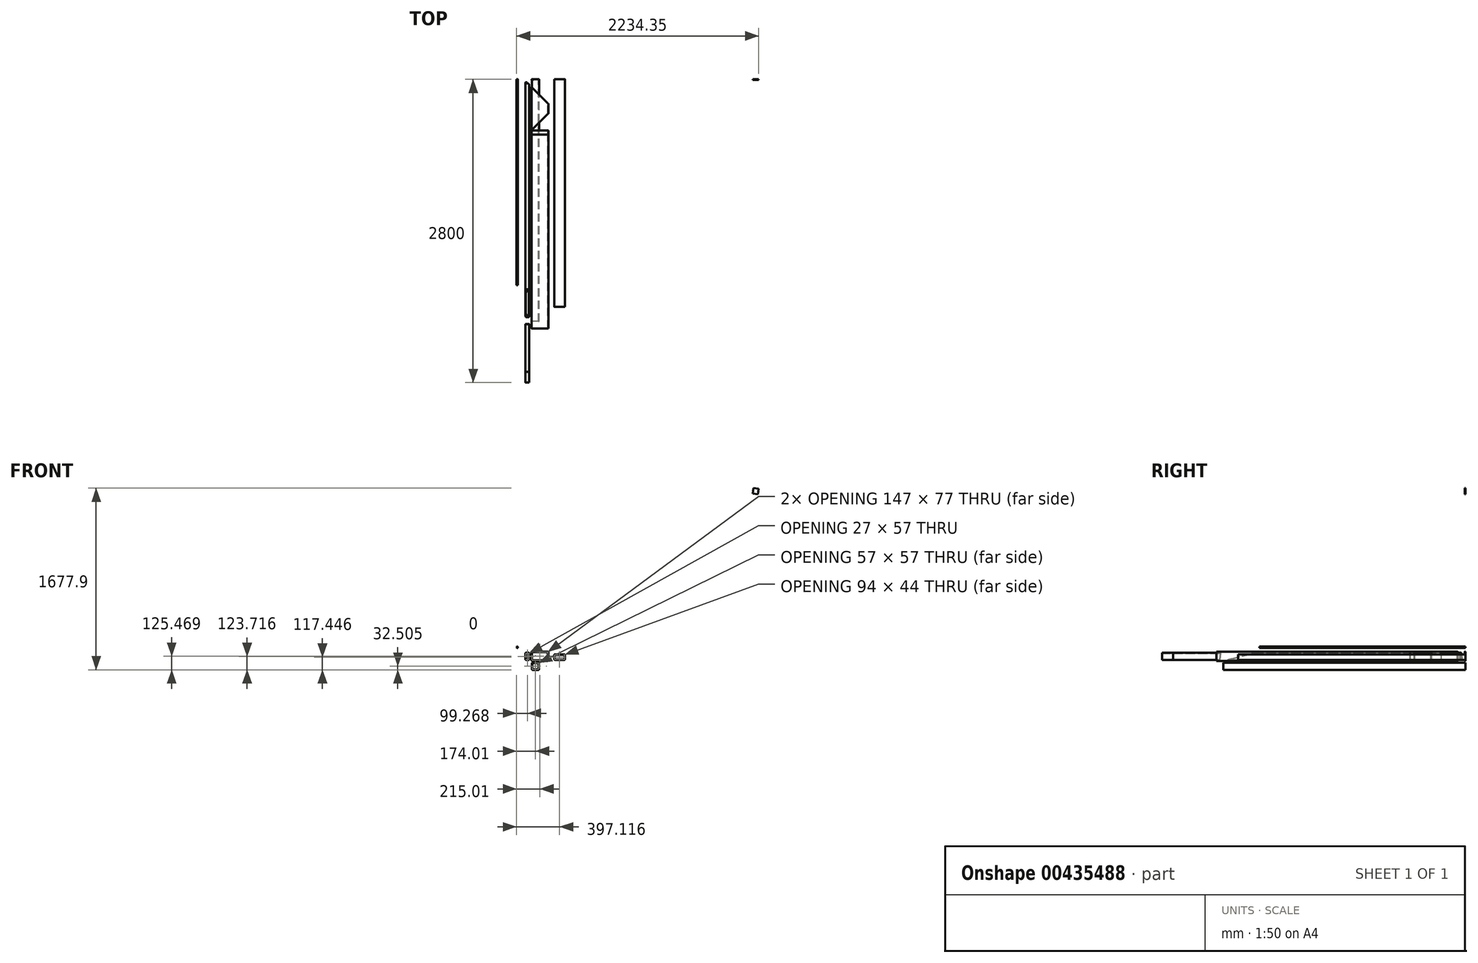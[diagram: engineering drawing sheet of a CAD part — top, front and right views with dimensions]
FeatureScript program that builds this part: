
annotation { "Feature Type Name" : "Feature", "Feature Type Description" : "" }
export const myFeature = defineFeature(function(context is Context, id is Id, definition is map)
    precondition{}
    {
        {
            var Q0;
            Q0=qCreatedBy(makeId("Front.planeOp"),FACE);
            var sketch = newSketch(context, id + "F0", { "sketchPlane" : qUnion([Q0])});
            skLineSegment(sketch, "E0.bottom", {"start": v(-54.74, 100.92) * mm, "end": v(-29.74, 100.92) * mm});
            skLineSegment(sketch, "E0.left", {"start": v(-59.74, 95.92) * mm, "end": v(-59.74, 40.92) * mm});
            skLineSegment(sketch, "E0.right", {"start": v(-24.74, 95.92) * mm, "end": v(-24.74, 40.92) * mm});
            skLineSegment(sketch, "E1.bottom", {"start": v(1, 27.67) * mm, "end": v(146, 27.67) * mm});
            skLineSegment(sketch, "E1.top", {"start": v(1, 112.67) * mm, "end": v(146, 112.67) * mm});
            skLineSegment(sketch, "E1.left", {"start": v(-4, 32.67) * mm, "end": v(-4, 107.67) * mm});
            skLineSegment(sketch, "E1.right", {"start": v(151, 32.67) * mm, "end": v(151, 107.67) * mm});
            skLineSegment(sketch, "E2.bottom", {"start": v(-50.74, 39.92) * mm, "end": v(-33.74, 39.92) * mm});
            skLineSegment(sketch, "E2.top", {"start": v(-50.74, 96.92) * mm, "end": v(-33.74, 96.92) * mm});
            skLineSegment(sketch, "E2.left", {"start": v(-55.74, 44.92) * mm, "end": v(-55.74, 91.92) * mm});
            skLineSegment(sketch, "E2.right", {"start": v(-28.74, 44.92) * mm, "end": v(-28.74, 91.92) * mm});
            skLineSegment(sketch, "E3", {"start": v(-54.74, 35.92) * mm, "end": v(-29.74, 35.92) * mm});
            skPoint(sketch, "E4.visualSharp", {"position": v(-59.74, 35.92) * mm});
            skArc(sketch, "E4.filletArc", {"start": v(-59.74, 40.92) * mm, "mid": v(-58.28, 37.38) * mm, "end": v(-54.74, 35.92) * mm});
            skPoint(sketch, "E5.visualSharp", {"position": v(-24.74, 35.92) * mm});
            skArc(sketch, "E5.filletArc", {"start": v(-29.74, 35.92) * mm, "mid": v(-26.2, 37.38) * mm, "end": v(-24.74, 40.92) * mm});
            skPoint(sketch, "E6.visualSharp", {"position": v(-28.74, 39.92) * mm});
            skArc(sketch, "E6.filletArc", {"start": v(-33.74, 39.92) * mm, "mid": v(-30.2, 41.38) * mm, "end": v(-28.74, 44.92) * mm});
            skPoint(sketch, "E7.visualSharp", {"position": v(-55.74, 39.92) * mm});
            skArc(sketch, "E7.filletArc", {"start": v(-55.74, 44.92) * mm, "mid": v(-54.28, 41.38) * mm, "end": v(-50.74, 39.92) * mm});
            skPoint(sketch, "E8.visualSharp", {"position": v(-55.74, 96.92) * mm});
            skArc(sketch, "E8.filletArc", {"start": v(-50.74, 96.92) * mm, "mid": v(-54.28, 95.45) * mm, "end": v(-55.74, 91.92) * mm});
            skPoint(sketch, "E9.visualSharp", {"position": v(-59.74, 100.92) * mm});
            skArc(sketch, "E9.filletArc", {"start": v(-54.74, 100.92) * mm, "mid": v(-58.28, 99.45) * mm, "end": v(-59.74, 95.92) * mm});
            skPoint(sketch, "E10.visualSharp", {"position": v(-28.74, 96.92) * mm});
            skArc(sketch, "E10.filletArc", {"start": v(-28.74, 91.92) * mm, "mid": v(-30.2, 95.45) * mm, "end": v(-33.74, 96.92) * mm});
            skPoint(sketch, "E11.visualSharp", {"position": v(-24.74, 100.92) * mm});
            skArc(sketch, "E11.filletArc", {"start": v(-24.74, 95.92) * mm, "mid": v(-26.2, 99.45) * mm, "end": v(-29.74, 100.92) * mm});
            skLineSegment(sketch, "E12.bottom", {"start": v(142, 108.67) * mm, "end": v(5, 108.67) * mm});
            skLineSegment(sketch, "E12.top", {"start": v(142, 31.67) * mm, "end": v(5, 31.67) * mm});
            skLineSegment(sketch, "E12.left", {"start": v(147, 103.67) * mm, "end": v(147, 36.67) * mm});
            skLineSegment(sketch, "E12.right", {"start": v(0, 103.67) * mm, "end": v(0, 36.67) * mm});
            skPoint(sketch, "E13.visualSharp", {"position": v(147, 108.67) * mm});
            skArc(sketch, "E13.filletArc", {"start": v(147, 103.67) * mm, "mid": v(145.54, 107.2) * mm, "end": v(142, 108.67) * mm});
            skPoint(sketch, "E14.visualSharp", {"position": v(151, 112.67) * mm});
            skArc(sketch, "E14.filletArc", {"start": v(151, 107.67) * mm, "mid": v(149.54, 111.2) * mm, "end": v(146, 112.67) * mm});
            skPoint(sketch, "E15.visualSharp", {"position": v(147, 31.67) * mm});
            skArc(sketch, "E15.filletArc", {"start": v(142, 31.67) * mm, "mid": v(145.54, 33.13) * mm, "end": v(147, 36.67) * mm});
            skPoint(sketch, "E16.visualSharp", {"position": v(151, 27.67) * mm});
            skArc(sketch, "E16.filletArc", {"start": v(146, 27.67) * mm, "mid": v(149.54, 29.13) * mm, "end": v(151, 32.67) * mm});
            skPoint(sketch, "E17.visualSharp", {"position": v(0, 31.67) * mm});
            skArc(sketch, "E17.filletArc", {"start": v(0, 36.67) * mm, "mid": v(1.46, 33.13) * mm, "end": v(5, 31.67) * mm});
            skPoint(sketch, "E18.visualSharp", {"position": v(-4, 27.67) * mm});
            skArc(sketch, "E18.filletArc", {"start": v(-4, 32.67) * mm, "mid": v(-2.54, 29.13) * mm, "end": v(1, 27.67) * mm});
            skPoint(sketch, "E19.visualSharp", {"position": v(0, 108.67) * mm});
            skArc(sketch, "E19.filletArc", {"start": v(5, 108.67) * mm, "mid": v(1.46, 107.2) * mm, "end": v(0, 103.67) * mm});
            skPoint(sketch, "E20.visualSharp", {"position": v(-4, 112.67) * mm});
            skArc(sketch, "E20.filletArc", {"start": v(1, 112.67) * mm, "mid": v(-2.54, 111.2) * mm, "end": v(-4, 107.67) * mm});
            skLineSegment(sketch, "E21.bottom", {"start": v(-105.6, 102.74) * mm, "end": v(-100.6, 102.74) * mm});
            skLineSegment(sketch, "E21.top", {"start": v(-105.6, 52.74) * mm, "end": v(-100.6, 52.74) * mm});
            skLineSegment(sketch, "E21.left", {"start": v(-105.6, 102.74) * mm, "end": v(-105.6, 52.74) * mm});
            skLineSegment(sketch, "E21.right", {"start": v(-100.6, 102.74) * mm, "end": v(-100.6, 52.74) * mm});
            skCircle(sketch, "E22", {"center": v(-135.5, 152.96) * mm, "radius": 6 * mm});
            skLineSegment(sketch, "E23", {"start": v(442.6, -372.53) * mm, "end": v(508.1, -372.53) * mm});
            skLineSegment(sketch, "E24", {"start": v(742.6, 1777.47) * mm, "end": v(710.1, 1777.47) * mm});
            skLineSegment(sketch, "E25", {"start": v(710.1, 1777.47) * mm, "end": v(775.1, 1777.47) * mm});
            skLineSegment(sketch, "E26", {"start": v(742.6, 1777.47) * mm, "end": v(775.1, 1777.47) * mm});
            skLineSegment(sketch, "E27", {"start": v(775.1, 1777.47) * mm, "end": v(710.1, 1777.47) * mm});
            skPoint(sketch, "E28.start.orphan", {"position": v(977.6, -372.53) * mm});
            skPoint(sketch, "E29.end.orphan", {"position": v(1042.6, -372.53) * mm});
            skLineSegment(sketch, "E30", {"start": v(742.6, 1777.47) * mm, "end": v(742.6, 1919.14) * mm});
            skLineSegment(sketch, "E31", {"start": v(742.6, 1919.14) * mm, "end": v(741.04, 1777.47) * mm});
            skPoint(sketch, "E32.end.orphan", {"position": v(508.1, -372.53) * mm});
            skPoint(sketch, "E33.trimOffspring.end.orphan", {"position": v(710.1, -1044.25) * mm});
            skLineSegment(sketch, "E34", {"start": v(1952.78, 1421.83) * mm, "end": v(2252.78, 1421.83) * mm});
            skLineSegment(sketch, "E35", {"start": v(2252.78, 1421.83) * mm, "end": v(2552.78, 1421.83) * mm});
            skLineSegment(sketch, "E36", {"start": v(2252.78, 3572.34) * mm, "end": v(2285.53, 3572.34) * mm});
            skLineSegment(sketch, "E37", {"start": v(2252.78, 3572.34) * mm, "end": v(2220.03, 3572.34) * mm});
            skLineSegment(sketch, "E38", {"start": v(2220.03, 3572.34) * mm, "end": v(1952.78, 1421.83) * mm});
            skLineSegment(sketch, "E39", {"start": v(2018.28, 1421.83) * mm, "end": v(2285.53, 3572.34) * mm});
            skLineSegment(sketch, "E40", {"start": v(2285.53, 3572.34) * mm, "end": v(2552.78, 1421.83) * mm});
            skLineSegment(sketch, "E41", {"start": v(2738.77, 1353.7) * mm, "end": v(2738.77, 1582.44) * mm});
            skLineSegment(sketch, "E42", {"start": v(2487.28, 1421.83) * mm, "end": v(2252.78, 3308.8) * mm});
            skLineSegment(sketch, "E43", {"start": v(2037.06, 1572.98) * mm, "end": v(2086.68, 1566.81) * mm});
            skLineSegment(sketch, "E44", {"start": v(2086.68, 1566.81) * mm, "end": v(2092.84, 1616.43) * mm});
            skLineSegment(sketch, "E45", {"start": v(2092.84, 1616.43) * mm, "end": v(2043.23, 1622.6) * mm});
            skLineSegment(sketch, "E46", {"start": v(2086.68, 1566.81) * mm, "end": v(2068.66, 1421.83) * mm});
            skLineSegment(sketch, "E47", {"start": v(2068.66, 1421.83) * mm, "end": v(2275.59, 3086.93) * mm});
            skLineSegment(sketch, "E48", {"start": v(2421.77, 1948.91) * mm, "end": v(2372.16, 1942.74) * mm});
            skLineSegment(sketch, "E49", {"start": v(2372.16, 1942.74) * mm, "end": v(2366, 1992.36) * mm});
            skLineSegment(sketch, "E50", {"start": v(2366, 1992.36) * mm, "end": v(2415.6, 1998.53) * mm});
            skLineSegment(sketch, "E51", {"start": v(2366, 1992.36) * mm, "end": v(2436.9, 1421.83) * mm});
            skLineSegment(sketch, "E52", {"start": v(2436.9, 1421.83) * mm, "end": v(2252.78, 2903.37) * mm});
            skSolve(sketch);
        }
        {
            var Q0;
            Q0=makeQuery(id+"F0.imprint","IMPRINT",FACE,{"disambiguationData":[TD([[makeQuery(id+"F0.imprint","IMPRINT",EDGE,{"derivedFrom":sQuery(id+"F0.wireOp",EDGE,"E1.bottom")}),1.0]])]});
            extrude(context, id + "F1", {"entities" : qUnion([Q0]), "depth" : 2300 * mm, "offsetDistance" : 25 * mm});
        }
        {
            var Q0;
            Q0=makeQuery(id+"F0.imprint","IMPRINT",FACE,{"disambiguationData":[TD([[makeQuery(id+"F0.imprint","IMPRINT",EDGE,{"derivedFrom":sQuery(id+"F0.wireOp",EDGE,"E0.bottom")}),-1.0]])]});
            extrude(context, id + "F2", {"entities" : qUnion([Q0]), "depth" : 2800 * mm});
        }
        {
            var Q0;
            Q0=makeQuery(id+"F0.imprint","IMPRINT",FACE,{"disambiguationData":[TD([[makeQuery(id+"F0.imprint","IMPRINT",EDGE,{"derivedFrom":sQuery(id+"F0.wireOp",EDGE,"E0.bottom")}),-1.0]])]});
            extrude(context, id + "F3", {"entities" : qUnion([Q0]), "depth" : 2700 * mm});
        }
        {
            var Q0;
            Q0=makeQuery(id+"F0.imprint","IMPRINT",FACE,{"disambiguationData":[TD([[makeQuery(id+"F0.imprint","IMPRINT",EDGE,{"derivedFrom":sQuery(id+"F0.wireOp",EDGE,"E0.bottom")}),-1.0]])]});
            extrude(context, id + "F4", {"entities" : qUnion([Q0]), "depth" : 2230 * mm});
        }
        {
            var Q0;
            Q0=makeQuery(id+"F0.imprint","IMPRINT",FACE,{"disambiguationData":[TD([[makeQuery(id+"F0.imprint","IMPRINT",EDGE,{"derivedFrom":sQuery(id+"F0.wireOp",EDGE,"E0.bottom")}),-1.0]])]});
            extrude(context, id + "F5", {"entities" : qUnion([Q0]), "depth" : 2200 * mm});
        }
        {
            var Q0;
            Q0=makeQuery(id+"F5.opExtrude","SWEPT_FACE",FACE,{"disambiguationData":[OSD([sQuery(id+"F0.wireOp",EDGE,"E0.right")])]});
            var sketch = newSketch(context, id + "F6", { "sketchPlane" : qUnion([Q0])});
            skLineSegment(sketch, "E53", {"start": v(-2188.64, 40.92) * mm, "end": v(-2149, 50.93) * mm});
            skLineSegment(sketch, "E54", {"start": v(-2149, 50.93) * mm, "end": v(-2188.64, 40.92) * mm});
            skLineSegment(sketch, "E55", {"start": v(-2239.78, 24.91) * mm, "end": v(-1867.66, 118.85) * mm});
            skLineSegment(sketch, "E56.top", {"start": v(-2239.78, 123.37) * mm, "end": v(-1867.66, 123.37) * mm});
            skLineSegment(sketch, "E56.left", {"start": v(-2239.78, 24.91) * mm, "end": v(-2239.78, 123.37) * mm});
            skLineSegment(sketch, "E56.right", {"start": v(-1867.66, 118.85) * mm, "end": v(-1867.66, 123.37) * mm});
            skLineSegment(sketch, "E57", {"start": v(-65.35, 40.92) * mm, "end": v(-65.35, 95.92) * mm});
            skLineSegment(sketch, "E58", {"start": v(-65.35, 95.92) * mm, "end": v(-59.5, 48.5) * mm});
            skSolve(sketch);
        }
        {
            var Q0;
            Q0 = qSketchRegion(id + "F6", true);
            extrude(context, id + "F7", {"entities" : qUnion([Q0]), "operationType" : NewBodyOperationType.REMOVE, "oppositeDirection" : true, "depth" : 65 * mm});
        }
        {
            var Q0;
            Q0=makeQuery(id+"F5.opExtrude","SWEPT_FACE",FACE,{"disambiguationData":[OSD([sQuery(id+"F0.wireOp",EDGE,"E3")])]});
            var sketch = newSketch(context, id + "F8", { "sketchPlane" : qUnion([Q0])});
            skLineSegment(sketch, "E59", {"start": v(-42.24, 2196.2) * mm, "end": v(-42.24, 29.2) * mm});
            skLineSegment(sketch, "E60", {"start": v(-42.24, 29.2) * mm, "end": v(-67.64, 29.2) * mm});
            skLineSegment(sketch, "E61.bottom", {"start": v(-67.64, 29.2) * mm, "end": v(-16.84, 29.2) * mm});
            skLineSegment(sketch, "E61.top", {"start": v(-67.64, -7.9) * mm, "end": v(-16.84, -7.9) * mm});
            skLineSegment(sketch, "E61.left", {"start": v(-67.64, 29.2) * mm, "end": v(-67.64, -7.9) * mm});
            skLineSegment(sketch, "E61.right", {"start": v(-16.84, 29.2) * mm, "end": v(-16.84, -7.9) * mm});
            skSolve(sketch);
        }
        {
            var Q0;
            Q0 = qSketchRegion(id + "F8", true);
            extrude(context, id + "F9", {"entities" : qUnion([Q0]), "operationType" : NewBodyOperationType.REMOVE, "oppositeDirection" : true, "depth" : 218 * mm});
        }
        {
            var Q0;
            Q0=makeQuery(id+"F5.opExtrude","SWEPT_FACE",FACE,{"disambiguationData":[OSD([sQuery(id+"F0.wireOp",EDGE,"E0.right")])]});
            var sketch = newSketch(context, id + "F10", { "sketchPlane" : qUnion([Q0])});
            skLineSegment(sketch, "E62", {"start": v(-29.2, 40.92) * mm, "end": v(-29.2, 35.92) * mm});
            skLineSegment(sketch, "E63", {"start": v(-29.2, 35.92) * mm, "end": v(-31.78, 56.74) * mm});
            skLineSegment(sketch, "E64", {"start": v(-29.2, 35.92) * mm, "end": v(-37.8, 105.2) * mm});
            skLineSegment(sketch, "E65", {"start": v(-37.8, 105.2) * mm, "end": v(-13.27, 108.25) * mm});
            skLineSegment(sketch, "E66", {"start": v(-13.27, 108.25) * mm, "end": v(-29.2, 35.92) * mm});
            skLineSegment(sketch, "E67", {"start": v(-2210.13, 148.78) * mm, "end": v(-2253.16, 154.06) * mm});
            skLineSegment(sketch, "E68", {"start": v(-2253.16, 154.06) * mm, "end": v(-2270.71, 11.1) * mm});
            skLineSegment(sketch, "E69", {"start": v(-2270.71, 11.1) * mm, "end": v(-2203.3, 2.83) * mm});
            skLineSegment(sketch, "E70", {"start": v(-2203.3, 2.83) * mm, "end": v(-2196.2, 35.92) * mm});
            skLineSegment(sketch, "E71", {"start": v(-2196.2, 35.92) * mm, "end": v(-2217.53, 208.7) * mm});
            skSolve(sketch);
        }
        {
            var Q0;
            Q0 = qSketchRegion(id + "F10", true);
            extrude(context, id + "F11", {"entities" : qUnion([Q0]), "operationType" : NewBodyOperationType.REMOVE, "oppositeDirection" : true, "depth" : 47.9 * mm});
        }
        {
            var Q0;
            Q0=makeQuery(id+"F0.imprint","IMPRINT",FACE,{"disambiguationData":[TD([[makeQuery(id+"F0.imprint","IMPRINT",EDGE,{"derivedFrom":sQuery(id+"F0.wireOp",EDGE,"E0.bottom")}),-1.0]])]});
            extrude(context, id + "F12", {"entities" : qUnion([Q0]), "depth" : 3000 * mm});
        }
        {
            var Q0;
            Q0 = qSketchRegion(id + "F10", true);
            extrude(context, id + "F13", {"entities" : qUnion([Q0]), "operationType" : NewBodyOperationType.REMOVE, "oppositeDirection" : true, "depth" : 73 * mm});
        }
        {
            var Q0;
            Q0=makeQuery(id+"F13.boolean.opBoolean","SPLIT",BODY,{"disambiguationData":[OD(0.0)],"derivedFrom":makeQuery(id+"F12.opExtrude","SWEPT_BODY",BODY,{"disambiguationData":[OSD([sQuery(id+"F0.wireOp",EDGE,"E0.bottom"),sQuery(id+"F0.wireOp",EDGE,"E0.left"),sQuery(id+"F0.wireOp",EDGE,"E0.right"),sQuery(id+"F0.wireOp",EDGE,"E2.bottom"),sQuery(id+"F0.wireOp",EDGE,"E2.top"),sQuery(id+"F0.wireOp",EDGE,"E2.left"),sQuery(id+"F0.wireOp",EDGE,"E2.right"),sQuery(id+"F0.wireOp",EDGE,"E3"),sQuery(id+"F0.wireOp",EDGE,"E4.filletArc"),sQuery(id+"F0.wireOp",EDGE,"E5.filletArc"),sQuery(id+"F0.wireOp",EDGE,"E6.filletArc"),sQuery(id+"F0.wireOp",EDGE,"E7.filletArc"),sQuery(id+"F0.wireOp",EDGE,"E8.filletArc"),sQuery(id+"F0.wireOp",EDGE,"E9.filletArc"),sQuery(id+"F0.wireOp",EDGE,"E10.filletArc"),sQuery(id+"F0.wireOp",EDGE,"E11.filletArc")])]})});
            deleteBodies(context, id + "F14", {"entities" : qUnion([Q0])});
        }
        {
            var Q0;
            Q0=makeQuery(id+"F0.imprint","IMPRINT",FACE,{"disambiguationData":[TD([[makeQuery(id+"F0.imprint","IMPRINT",EDGE,{"derivedFrom":sQuery(id+"F0.wireOp",EDGE,"E22")}),1.0]])]});
            extrude(context, id + "F15", {"entities" : qUnion([Q0]), "depth" : 1900.9 * mm});
        }
        {
            var Q0;
            {var subQ0=sQuery(id+"F0.wireOp",EDGE,"E43");Q0=makeQuery(id+"F0.imprint","IMPRINT",FACE,{"disambiguationData":[TD([[makeQuery(id+"F0.imprint","IMPRINT",EDGE,{"derivedFrom":subQ0}),1.0]])]});}
            extrude(context, id + "F16", {"entities" : qUnion([Q0]), "depth" : 5 * mm});
        }
        {
            var Q0;
            Q0=makeQuery(id+"F0.imprint","IMPRINT",FACE,{"disambiguationData":[TD([[makeQuery(id+"F0.imprint","IMPRINT",EDGE,{"derivedFrom":sQuery(id+"F0.wireOp",EDGE,"E1.bottom")}),1.0]])]});
            extrude(context, id + "F17", {"entities" : qUnion([Q0]), "depth" : 510 * mm});
        }
        {
            var Q0;
            Q0=makeQuery(id+"F17.opExtrude","SWEPT_FACE",FACE,{"disambiguationData":[OSD([sQuery(id+"F0.wireOp",EDGE,"E1.top")])]});
            var sketch = newSketch(context, id + "F18", { "sketchPlane" : qUnion([Q0])});
            skLineSegment(sketch, "E72", {"start": v(146, -220.74) * mm, "end": v(-59.9, -14.83) * mm});
            skLineSegment(sketch, "E73", {"start": v(146, -320.74) * mm, "end": v(-7.13, -473.86) * mm});
            skLineSegment(sketch, "E74", {"start": v(-7.13, -473.86) * mm, "end": v(185.32, -473.86) * mm});
            skLineSegment(sketch, "E75", {"start": v(185.32, -473.86) * mm, "end": v(185.32, 27.31) * mm});
            skLineSegment(sketch, "E76", {"start": v(185.32, 27.31) * mm, "end": v(-59.9, -14.83) * mm});
            skLineSegment(sketch, "E77", {"start": v(146, -220.74) * mm, "end": v(162.83, -237.57) * mm});
            skLineSegment(sketch, "E78", {"start": v(146, -320.74) * mm, "end": v(165.64, -301.1) * mm});
            skLineSegment(sketch, "E79", {"start": v(165.64, -301.1) * mm, "end": v(162.83, -237.57) * mm});
            skSolve(sketch);
        }
        {
            var Q0;
            Q0 = qSketchRegion(id + "F18", true);
            extrude(context, id + "F19", {"entities" : qUnion([Q0]), "operationType" : NewBodyOperationType.REMOVE, "oppositeDirection" : true, "depth" : 125 * mm});
        }
        {
            var Q0;
            Q0=qCreatedBy(makeId("Front.planeOp"),FACE);
            var sketch = newSketch(context, id + "F20", { "sketchPlane" : qUnion([Q0])});
            skLineSegment(sketch, "E80.bottom", {"start": v(60, 9.7) * mm, "end": v(5, 9.7) * mm});
            skLineSegment(sketch, "E80.top", {"start": v(60, -55.3) * mm, "end": v(5, -55.3) * mm});
            skLineSegment(sketch, "E80.left", {"start": v(65, 4.7) * mm, "end": v(65, -50.3) * mm});
            skLineSegment(sketch, "E80.right", {"start": v(0, 4.7) * mm, "end": v(0, -50.3) * mm});
            skLineSegment(sketch, "E81.bottom", {"start": v(56, 5.7) * mm, "end": v(9, 5.7) * mm});
            skLineSegment(sketch, "E81.top", {"start": v(56, -51.3) * mm, "end": v(9, -51.3) * mm});
            skLineSegment(sketch, "E81.left", {"start": v(61, 0.7) * mm, "end": v(61, -46.3) * mm});
            skLineSegment(sketch, "E81.right", {"start": v(4, 0.7) * mm, "end": v(4, -46.3) * mm});
            skPoint(sketch, "E82.visualSharp", {"position": v(61, 5.7) * mm});
            skArc(sketch, "E82.filletArc", {"start": v(61, 0.7) * mm, "mid": v(59.54, 4.24) * mm, "end": v(56, 5.7) * mm});
            skPoint(sketch, "E83.visualSharp", {"position": v(65, 9.7) * mm});
            skArc(sketch, "E83.filletArc", {"start": v(65, 4.7) * mm, "mid": v(63.54, 8.24) * mm, "end": v(60, 9.7) * mm});
            skPoint(sketch, "E84.visualSharp", {"position": v(0, 9.7) * mm});
            skArc(sketch, "E84.filletArc", {"start": v(5, 9.7) * mm, "mid": v(1.46, 8.24) * mm, "end": v(0, 4.7) * mm});
            skPoint(sketch, "E85.visualSharp", {"position": v(4, 5.7) * mm});
            skArc(sketch, "E85.filletArc", {"start": v(9, 5.7) * mm, "mid": v(5.46, 4.24) * mm, "end": v(4, 0.7) * mm});
            skPoint(sketch, "E86.visualSharp", {"position": v(4, -51.3) * mm});
            skArc(sketch, "E86.filletArc", {"start": v(4, -46.3) * mm, "mid": v(5.46, -49.83) * mm, "end": v(9, -51.3) * mm});
            skPoint(sketch, "E87.visualSharp", {"position": v(0, -55.3) * mm});
            skArc(sketch, "E87.filletArc", {"start": v(0, -50.3) * mm, "mid": v(1.46, -53.83) * mm, "end": v(5, -55.3) * mm});
            skPoint(sketch, "E88.visualSharp", {"position": v(61, -51.3) * mm});
            skArc(sketch, "E88.filletArc", {"start": v(56, -51.3) * mm, "mid": v(59.54, -49.83) * mm, "end": v(61, -46.3) * mm});
            skPoint(sketch, "E89.visualSharp", {"position": v(65, -55.3) * mm});
            skArc(sketch, "E89.filletArc", {"start": v(60, -55.3) * mm, "mid": v(63.54, -53.83) * mm, "end": v(65, -50.3) * mm});
            skPoint(sketch, "E90.end.orphan", {"position": v(4, -46.62) * mm});
            skPoint(sketch, "E91.end.orphan", {"position": v(15.37, 5.7) * mm});
            skPoint(sketch, "E92.end.orphan", {"position": v(61, -5.88) * mm});
            skPoint(sketch, "E93.end.orphan", {"position": v(34.59, -51.3) * mm});
            skSolve(sketch);
        }
        {
            var Q0;
            Q0 = qSketchRegion(id + "F20", true);
            extrude(context, id + "F21", {"entities" : qUnion([Q0]), "depth" : 2235 * mm});
        }
        {
            var Q0;
            Q0=qCreatedBy(makeId("Front.planeOp"),FACE);
            var sketch = newSketch(context, id + "F22", { "sketchPlane" : qUnion([Q0])});
            skLineSegment(sketch, "E94.bottom", {"start": v(300.6, 87.15) * mm, "end": v(210.6, 87.15) * mm});
            skLineSegment(sketch, "E94.top", {"start": v(300.6, 37.15) * mm, "end": v(210.6, 37.15) * mm});
            skLineSegment(sketch, "E94.left", {"start": v(305.6, 82.15) * mm, "end": v(305.6, 42.15) * mm});
            skLineSegment(sketch, "E94.right", {"start": v(205.6, 82.15) * mm, "end": v(205.6, 42.15) * mm});
            skLineSegment(sketch, "E95", {"start": v(305.6, 62.15) * mm, "end": v(302.6, 62.15) * mm});
            skLineSegment(sketch, "E96", {"start": v(258.58, 37.15) * mm, "end": v(258.58, 40.15) * mm});
            skLineSegment(sketch, "E97", {"start": v(205.6, 42.85) * mm, "end": v(208.6, 42.85) * mm});
            skLineSegment(sketch, "E98", {"start": v(253.83, 87.15) * mm, "end": v(253.83, 84.15) * mm});
            skLineSegment(sketch, "E99.bottom", {"start": v(297.6, 84.15) * mm, "end": v(213.6, 84.15) * mm});
            skLineSegment(sketch, "E99.top", {"start": v(297.6, 40.15) * mm, "end": v(213.6, 40.15) * mm});
            skLineSegment(sketch, "E99.left", {"start": v(302.6, 79.15) * mm, "end": v(302.6, 45.15) * mm});
            skLineSegment(sketch, "E99.right", {"start": v(208.6, 79.15) * mm, "end": v(208.6, 45.15) * mm});
            skPoint(sketch, "E100.visualSharp", {"position": v(305.6, 87.15) * mm});
            skArc(sketch, "E100.filletArc", {"start": v(305.6, 82.15) * mm, "mid": v(304.14, 85.68) * mm, "end": v(300.6, 87.15) * mm});
            skPoint(sketch, "E101.visualSharp", {"position": v(205.6, 87.15) * mm});
            skArc(sketch, "E101.filletArc", {"start": v(210.6, 87.15) * mm, "mid": v(207.07, 85.68) * mm, "end": v(205.6, 82.15) * mm});
            skPoint(sketch, "E102.visualSharp", {"position": v(208.6, 84.15) * mm});
            skArc(sketch, "E102.filletArc", {"start": v(213.6, 84.15) * mm, "mid": v(210.07, 82.68) * mm, "end": v(208.6, 79.15) * mm});
            skPoint(sketch, "E103.visualSharp", {"position": v(208.6, 40.15) * mm});
            skArc(sketch, "E103.filletArc", {"start": v(208.6, 45.15) * mm, "mid": v(210.07, 41.61) * mm, "end": v(213.6, 40.15) * mm});
            skPoint(sketch, "E104.visualSharp", {"position": v(205.6, 37.15) * mm});
            skArc(sketch, "E104.filletArc", {"start": v(205.6, 42.15) * mm, "mid": v(207.07, 38.61) * mm, "end": v(210.6, 37.15) * mm});
            skPoint(sketch, "E105.visualSharp", {"position": v(302.6, 40.15) * mm});
            skArc(sketch, "E105.filletArc", {"start": v(297.6, 40.15) * mm, "mid": v(301.14, 41.61) * mm, "end": v(302.6, 45.15) * mm});
            skPoint(sketch, "E106.visualSharp", {"position": v(305.6, 37.15) * mm});
            skArc(sketch, "E106.filletArc", {"start": v(300.6, 37.15) * mm, "mid": v(304.14, 38.61) * mm, "end": v(305.6, 42.15) * mm});
            skPoint(sketch, "E107.visualSharp", {"position": v(302.6, 84.15) * mm});
            skArc(sketch, "E107.filletArc", {"start": v(302.6, 79.15) * mm, "mid": v(301.14, 82.68) * mm, "end": v(297.6, 84.15) * mm});
            skSolve(sketch);
        }
        {
            var Q0;
            Q0 = qSketchRegion(id + "F22", true);
            extrude(context, id + "F23", {"entities" : qUnion([Q0]), "depth" : 2100 * mm});
        }
    });
